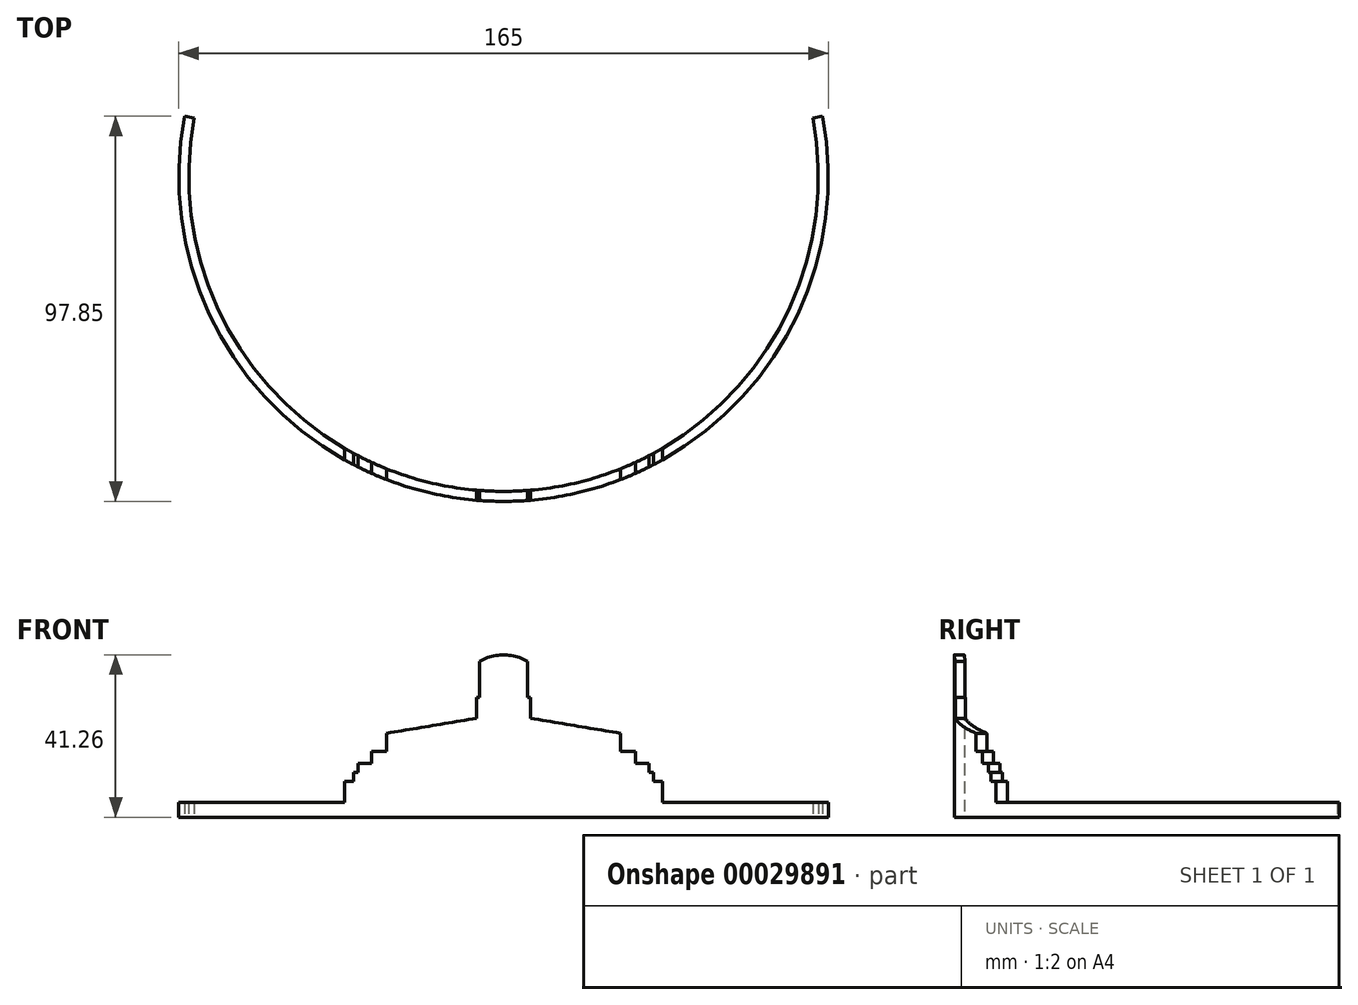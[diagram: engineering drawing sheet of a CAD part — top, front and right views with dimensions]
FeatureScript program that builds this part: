
annotation { "Feature Type Name" : "Feature", "Feature Type Description" : "" }
export const myFeature = defineFeature(function(context is Context, id is Id, definition is map)
    precondition{}
    {
        {
            var Q0;
            Q0=qCreatedBy(makeId("Front.planeOp"),FACE);
            var sketch = newSketch(context, id + "F0", { "sketchPlane" : qUnion([Q0])});
            skLineSegment(sketch, "E0", {"start": v(-67.31, 0) * mm, "end": v(67.31, 0) * mm});
            skLineSegment(sketch, "E1", {"start": v(67.31, 0) * mm, "end": v(67.31, 15.24) * mm});
            skLineSegment(sketch, "E2", {"start": v(67.31, 15.24) * mm, "end": v(63.5, 15.24) * mm});
            skLineSegment(sketch, "E3", {"start": v(63.5, 15.24) * mm, "end": v(63.5, 19.05) * mm});
            skLineSegment(sketch, "E4", {"start": v(63.5, 19.05) * mm, "end": v(61.6, 19.05) * mm});
            skLineSegment(sketch, "E5", {"start": v(61.6, 19.05) * mm, "end": v(61.6, 22.86) * mm});
            skLineSegment(sketch, "E6", {"start": v(61.6, 22.86) * mm, "end": v(55.88, 22.86) * mm});
            skLineSegment(sketch, "E7", {"start": v(55.88, 22.86) * mm, "end": v(55.88, 27.94) * mm});
            skLineSegment(sketch, "E8", {"start": v(55.88, 27.94) * mm, "end": v(49.53, 27.94) * mm});
            skLineSegment(sketch, "E9", {"start": v(49.53, 27.94) * mm, "end": v(49.53, 35.56) * mm});
            skLineSegment(sketch, "E10", {"start": v(49.53, 35.56) * mm, "end": v(11.43, 41.91) * mm});
            skLineSegment(sketch, "E11", {"start": v(11.43, 41.91) * mm, "end": v(11.43, 50.8) * mm});
            skLineSegment(sketch, "E12", {"start": v(11.43, 50.8) * mm, "end": v(10.16, 50.8) * mm});
            skLineSegment(sketch, "E13", {"start": v(10.16, 50.8) * mm, "end": v(10.16, 66.04) * mm});
            skLineSegment(sketch, "E14", {"start": v(10.16, 66.04) * mm, "end": v(0, 66.04) * mm, "construction": true});
            skLineSegment(sketch, "E15", {"start": v(0, 66.04) * mm, "end": v(0, 0) * mm, "construction": true});
            skLineSegment(sketch, "E16.MirrorCS", {"start": v(-10.16, 66.04) * mm, "end": v(0, 66.04) * mm, "construction": true});
            skLineSegment(sketch, "E17.MirrorCS", {"start": v(-10.16, 50.8) * mm, "end": v(-10.16, 66.04) * mm});
            skLineSegment(sketch, "E18.MirrorCS", {"start": v(-11.43, 41.91) * mm, "end": v(-11.43, 50.8) * mm});
            skLineSegment(sketch, "E19.MirrorCS", {"start": v(-49.53, 35.56) * mm, "end": v(-11.43, 41.91) * mm});
            skLineSegment(sketch, "E20.MirrorCS", {"start": v(-49.53, 27.94) * mm, "end": v(-49.53, 35.56) * mm});
            skLineSegment(sketch, "E21.MirrorCS", {"start": v(-55.88, 27.94) * mm, "end": v(-49.53, 27.94) * mm});
            skLineSegment(sketch, "E22.MirrorCS", {"start": v(-55.88, 22.86) * mm, "end": v(-55.88, 27.94) * mm});
            skLineSegment(sketch, "E23.MirrorCS", {"start": v(-61.6, 22.86) * mm, "end": v(-55.88, 22.86) * mm});
            skLineSegment(sketch, "E24.MirrorCS", {"start": v(-61.6, 19.05) * mm, "end": v(-61.6, 22.86) * mm});
            skLineSegment(sketch, "E25.MirrorCS", {"start": v(-63.5, 15.24) * mm, "end": v(-63.5, 19.05) * mm});
            skLineSegment(sketch, "E26.MirrorCS", {"start": v(-67.31, 15.24) * mm, "end": v(-63.5, 15.24) * mm});
            skLineSegment(sketch, "E27.MirrorCS", {"start": v(-67.31, 0) * mm, "end": v(-67.31, 15.24) * mm});
            skLineSegment(sketch, "E28", {"start": v(-63.5, 19.05) * mm, "end": v(-61.6, 19.05) * mm});
            skLineSegment(sketch, "E29", {"start": v(-10.16, 50.8) * mm, "end": v(-11.43, 50.8) * mm});
            skArc(sketch, "E30", {"start": v(10.16, 66.04) * mm, "mid": v(0, 68.76) * mm, "end": v(-10.16, 66.04) * mm});
            skSolve(sketch);
        }
        {
            var Q0;
            Q0=qCreatedBy(makeId("Top.planeOp"),FACE);
            var sketch = newSketch(context, id + "F1", { "sketchPlane" : qUnion([Q0])});
            skArc(sketch, "E31", {"start": v(-81.06, 97.85) * mm, "mid": v(0, 0) * mm, "end": v(81.06, 97.85) * mm});
            skArc(sketch, "E32.0", {"start": v(-78.56, 97.38) * mm, "mid": v(0, 2.54) * mm, "end": v(78.56, 97.38) * mm});
            skLineSegment(sketch, "E33", {"start": v(-78.56, 97.38) * mm, "end": v(-81.06, 97.85) * mm});
            skLineSegment(sketch, "E34", {"start": v(81.06, 97.85) * mm, "end": v(78.56, 97.38) * mm});
            skSolve(sketch);
        }
        {
            var Q0;
            Q0=qSketchRegion(id+"F0",true);
            extrude(context, id + "F2", {"entities" : qUnion([Q0]), "oppositeDirection" : true, "depth" : 48.53 * mm});
        }
        {
            var Q0;
            Q0=makeQuery(id+"F2.opExtrude","SWEPT_BODY",BODY,{"disambiguationData":[OSD([sQuery(id+"F0.wireOp",EDGE,"E0"),sQuery(id+"F0.wireOp",EDGE,"E1"),sQuery(id+"F0.wireOp",EDGE,"E2"),sQuery(id+"F0.wireOp",EDGE,"E3"),sQuery(id+"F0.wireOp",EDGE,"E4"),sQuery(id+"F0.wireOp",EDGE,"E5"),sQuery(id+"F0.wireOp",EDGE,"E6"),sQuery(id+"F0.wireOp",EDGE,"E7"),sQuery(id+"F0.wireOp",EDGE,"E8"),sQuery(id+"F0.wireOp",EDGE,"E9"),sQuery(id+"F0.wireOp",EDGE,"E10"),sQuery(id+"F0.wireOp",EDGE,"E11"),sQuery(id+"F0.wireOp",EDGE,"E12"),sQuery(id+"F0.wireOp",EDGE,"E13"),sQuery(id+"F0.wireOp",EDGE,"E17.MirrorCS"),sQuery(id+"F0.wireOp",EDGE,"E18.MirrorCS"),sQuery(id+"F0.wireOp",EDGE,"E19.MirrorCS"),sQuery(id+"F0.wireOp",EDGE,"E20.MirrorCS"),sQuery(id+"F0.wireOp",EDGE,"E21.MirrorCS"),sQuery(id+"F0.wireOp",EDGE,"E22.MirrorCS"),sQuery(id+"F0.wireOp",EDGE,"E23.MirrorCS"),sQuery(id+"F0.wireOp",EDGE,"E24.MirrorCS"),sQuery(id+"F0.wireOp",EDGE,"E25.MirrorCS"),sQuery(id+"F0.wireOp",EDGE,"E26.MirrorCS"),sQuery(id+"F0.wireOp",EDGE,"E27.MirrorCS"),sQuery(id+"F0.wireOp",EDGE,"E28"),sQuery(id+"F0.wireOp",EDGE,"E29"),sQuery(id+"F0.wireOp",EDGE,"E30")])]});
            var Q1;
            Q1=qCreatedBy(makeId("Origin.pointOp"),VERTEX);
            transform(context, id + "F3", {"entities" : qUnion([Q0]), "transformType" : TransformType.SCALE_UNIFORMLY, "scale" : .6, "makeCopy" : false, "scalePoint" : qUnion([Q1])});
        }
        {
            var Q0;
            Q0=qSketchRegion(id+"F1",true);
            extrude(context, id + "F4", {"entities" : qUnion([Q0]), "operationType" : NewBodyOperationType.INTERSECT, "depth" : 76.2 * mm});
        }
        {
            var Q0;
            Q0=qSketchRegion(id+"F1",true);
            var Q1;
            Q1=makeQuery(id+"F2.opExtrude","SWEPT_FACE",FACE,{"disambiguationData":[OSD([sQuery(id+"F0.wireOp",EDGE,"E26.MirrorCS")])]});
            extrude(context, id + "F5", {"entities" : qUnion([Q0]), "operationType" : NewBodyOperationType.ADD, "endBoundEntityFace" : qUnion([Q1]), "depth" : 3.8 * mm});
        }
    });
